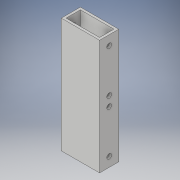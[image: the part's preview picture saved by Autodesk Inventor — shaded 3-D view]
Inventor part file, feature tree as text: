
AUTODESK INVENTOR PART (.ipt)
format: ipt  version: 2017 (Build 210142000, 142)  size: 121,344 bytes
history: native  units: in
note: dims shown in document units (in); Inventor stores cm internally (conversion verified against a paired STEP export)
features: sketch x2, extrude x1, hole x1
ambient origin geometry x8: Origin, YZ Plane, XZ Plane, XY Plane, X Axis, Y Axis, Z Axis, Center Point
bodies: Solid1 (feature_tree)
feature tree (4):
  extrude  "Extrusion1"  Depth=1.0in
  hole  "Hole1"  [1 undecoded]
  sketch  "Sketch1"  dims[d0=2.0in d1=1.0in]
  sketch  "Sketch2"  dims[d2=1.75in d3=0.75in d4=0.125in d5=0.125in d6=6.0in d7=0.0in d8=0.25in d9=0.25in d10=0.25in d11=0.5in d12=0.25in d13=0.75in d14=0.375in d15=0.25in d16=0.5635in d17=1.0in d18=0.8108in]
note: 1 required parameter value undecoded (feature->parameter linkage not recoverable at this tier; creation-order binding heuristic only, values carry confidence <= 0.55)
